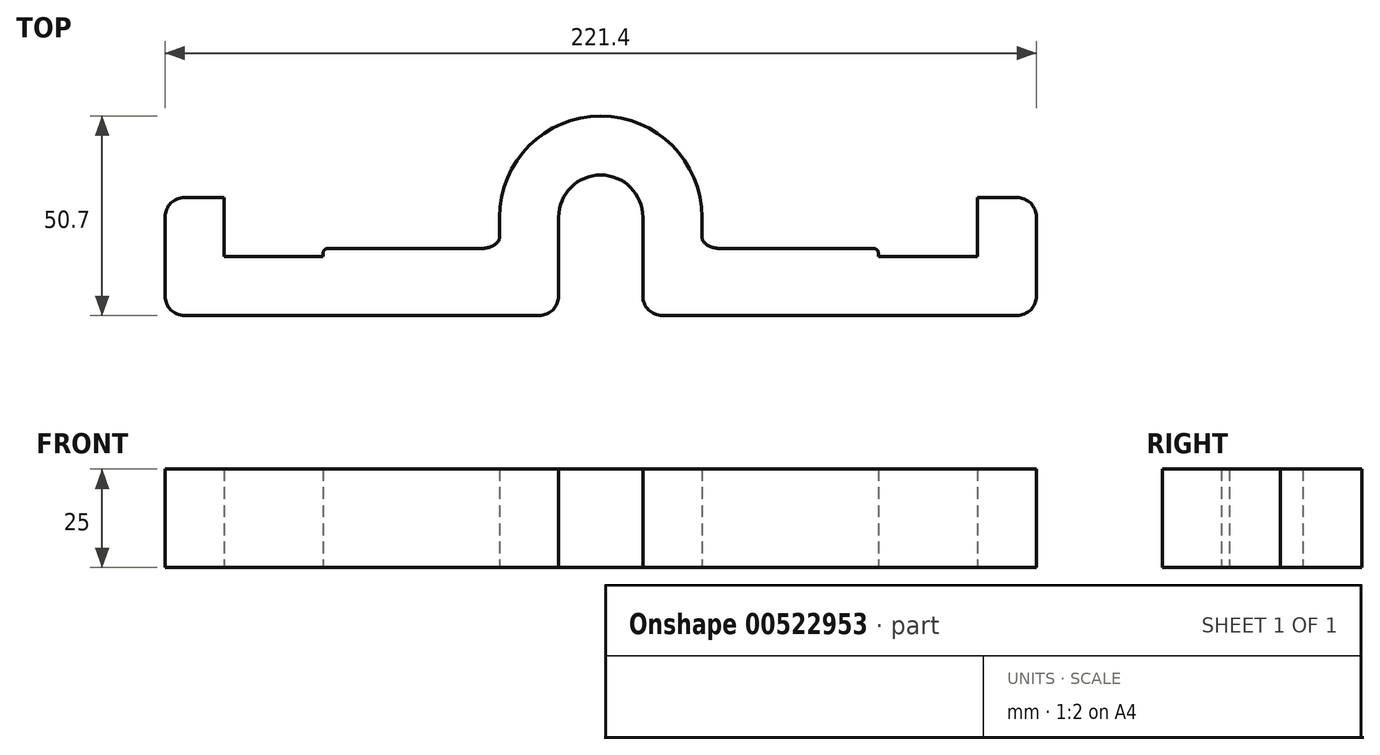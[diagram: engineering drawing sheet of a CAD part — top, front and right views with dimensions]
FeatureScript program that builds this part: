
annotation { "Feature Type Name" : "Feature", "Feature Type Description" : "" }
export const myFeature = defineFeature(function(context is Context, id is Id, definition is map)
    precondition{}
    {
        {
            var Q0;
            Q0=qCreatedBy(makeId("Top.planeOp"),FACE);
            var sketch = newSketch(context, id + "F0", { "sketchPlane" : qUnion([Q0])});
            skCircle(sketch, "E0", {"center": v(0, 0) * mm, "radius": 10.5 * mm, "construction": true});
            skCircle(sketch, "E1.0", {"center": v(0, 0) * mm, "radius": 10.7 * mm, "construction": true});
            skArc(sketch, "E2", {"start": v(10.7, 0) * mm, "mid": v(0, 10.7) * mm, "end": v(-10.7, 0) * mm});
            skLineSegment(sketch, "E3", {"start": v(-10.7, 0) * mm, "end": v(-10.7, -20) * mm});
            skLineSegment(sketch, "E4", {"start": v(-15.7, -25) * mm, "end": v(-105.7, -25) * mm});
            skPoint(sketch, "E5.visualSharp", {"position": v(-10.7, -25) * mm});
            skArc(sketch, "E5.filletArc", {"start": v(-15.7, -25) * mm, "mid": v(-12.16, -23.54) * mm, "end": v(-10.7, -20) * mm});
            skLineSegment(sketch, "E6.MirrorCS", {"start": v(10.7, 0) * mm, "end": v(10.7, -20) * mm});
            skArc(sketch, "E7.MirrorCS", {"start": v(15.7, -25) * mm, "mid": v(12.16, -23.54) * mm, "end": v(10.7, -20) * mm});
            skLineSegment(sketch, "E8.MirrorCS", {"start": v(15.7, -25) * mm, "end": v(105.7, -25) * mm});
            skLineSegment(sketch, "E9.0", {"start": v(70.5, -10) * mm, "end": v(95.7, -10) * mm});
            skLineSegment(sketch, "E9.1", {"start": v(-30.7, -10) * mm, "end": v(-70.5, -10) * mm, "construction": true});
            skLineSegment(sketch, "E9.2", {"start": v(-25.7, 0) * mm, "end": v(-25.7, -5) * mm});
            skArc(sketch, "E9.3", {"start": v(25.7, 0) * mm, "mid": v(0, 25.7) * mm, "end": v(-25.7, 0) * mm});
            skLineSegment(sketch, "E10", {"start": v(110.7, -10) * mm, "end": v(110.7, -20) * mm});
            skLineSegment(sketch, "E11", {"start": v(-110.7, -10) * mm, "end": v(-110.7, -20) * mm});
            skPoint(sketch, "E12.visualSharp", {"position": v(-25.7, -10) * mm});
            skArc(sketch, "E12.filletArc", {"start": v(-30.7, -10) * mm, "mid": v(-27.16, -8.54) * mm, "end": v(-25.7, -5) * mm, "construction": true});
            skLineSegment(sketch, "E13.top", {"start": v(-105.7, 5) * mm, "end": v(-95.7, 5) * mm});
            skLineSegment(sketch, "E13.left", {"start": v(-110.7, -10) * mm, "end": v(-110.7, 0) * mm});
            skLineSegment(sketch, "E13.right", {"start": v(-95.7, -10) * mm, "end": v(-95.7, 5) * mm});
            skLineSegment(sketch, "E14.MirrorCS", {"start": v(95.7, -10) * mm, "end": v(95.7, 5) * mm});
            skLineSegment(sketch, "E15.MirrorCS", {"start": v(105.7, 5) * mm, "end": v(95.7, 5) * mm});
            skLineSegment(sketch, "E16.MirrorCS", {"start": v(110.7, -10) * mm, "end": v(110.7, 0) * mm});
            skPoint(sketch, "E17.visualSharp", {"position": v(-110.7, -25) * mm});
            skArc(sketch, "E17.filletArc", {"start": v(-110.7, -20) * mm, "mid": v(-109.24, -23.54) * mm, "end": v(-105.7, -25) * mm});
            skPoint(sketch, "E18.visualSharp", {"position": v(110.7, -25) * mm});
            skArc(sketch, "E18.filletArc", {"start": v(105.7, -25) * mm, "mid": v(109.24, -23.54) * mm, "end": v(110.7, -20) * mm});
            skLineSegment(sketch, "E19", {"start": v(-70.5, -10) * mm, "end": v(-95.7, -10) * mm});
            skLineSegment(sketch, "E20.0", {"start": v(-30.7, -8) * mm, "end": v(-69.5, -8) * mm});
            skEllipticalArc(sketch, "E21", {});
            skLineSegment(sketch, "E22", {"start": v(-70.5, -9) * mm, "end": v(-70.5, -10) * mm});
            skEllipticalArc(sketch, "E23.MirrorCS", {});
            skLineSegment(sketch, "E24.MirrorCS", {"start": v(30.7, -8) * mm, "end": v(69.5, -8) * mm});
            skLineSegment(sketch, "E25.MirrorCS", {"start": v(70.5, -9) * mm, "end": v(70.5, -10) * mm});
            skPoint(sketch, "E26.visualSharp", {"position": v(-70.5, -8) * mm});
            skArc(sketch, "E26.filletArc", {"start": v(-69.5, -8) * mm, "mid": v(-70.2, -8.3) * mm, "end": v(-70.5, -9) * mm});
            skPoint(sketch, "E27.visualSharp", {"position": v(70.5, -8) * mm});
            skArc(sketch, "E27.filletArc", {"start": v(70.5, -9) * mm, "mid": v(70.2, -8.3) * mm, "end": v(69.5, -8) * mm});
            skPoint(sketch, "E28.visualSharp", {"position": v(-110.7, 5) * mm});
            skArc(sketch, "E28.filletArc", {"start": v(-105.7, 5) * mm, "mid": v(-109.24, 3.54) * mm, "end": v(-110.7, 0) * mm});
            skPoint(sketch, "E29.visualSharp", {"position": v(110.7, 5) * mm});
            skArc(sketch, "E29.filletArc", {"start": v(110.7, 0) * mm, "mid": v(109.24, 3.54) * mm, "end": v(105.7, 5) * mm});
            skLineSegment(sketch, "E30", {"start": v(25.7, 0) * mm, "end": v(25.7, -5) * mm});
            const initialGuessF0  = {"E21": [-0.0307, -0.005, 1, 0, 0.005, 0.003, 4.71238898038469, 0], "E23.MirrorCS": [0.0307, -0.005, -1, 0, 0.005, 0.003, 0, 1.5707963267948963]};
            skSetInitialGuess(sketch, initialGuessF0);
            skSolve(sketch);
        }
        {
            var Q0;
            Q0 = qSketchRegion(id + "F0", true);
            extrude(context, id + "F1", {"entities" : qUnion([Q0]), "depth" : 25 * mm, "offsetDistance" : 25 * mm});
        }
    });
